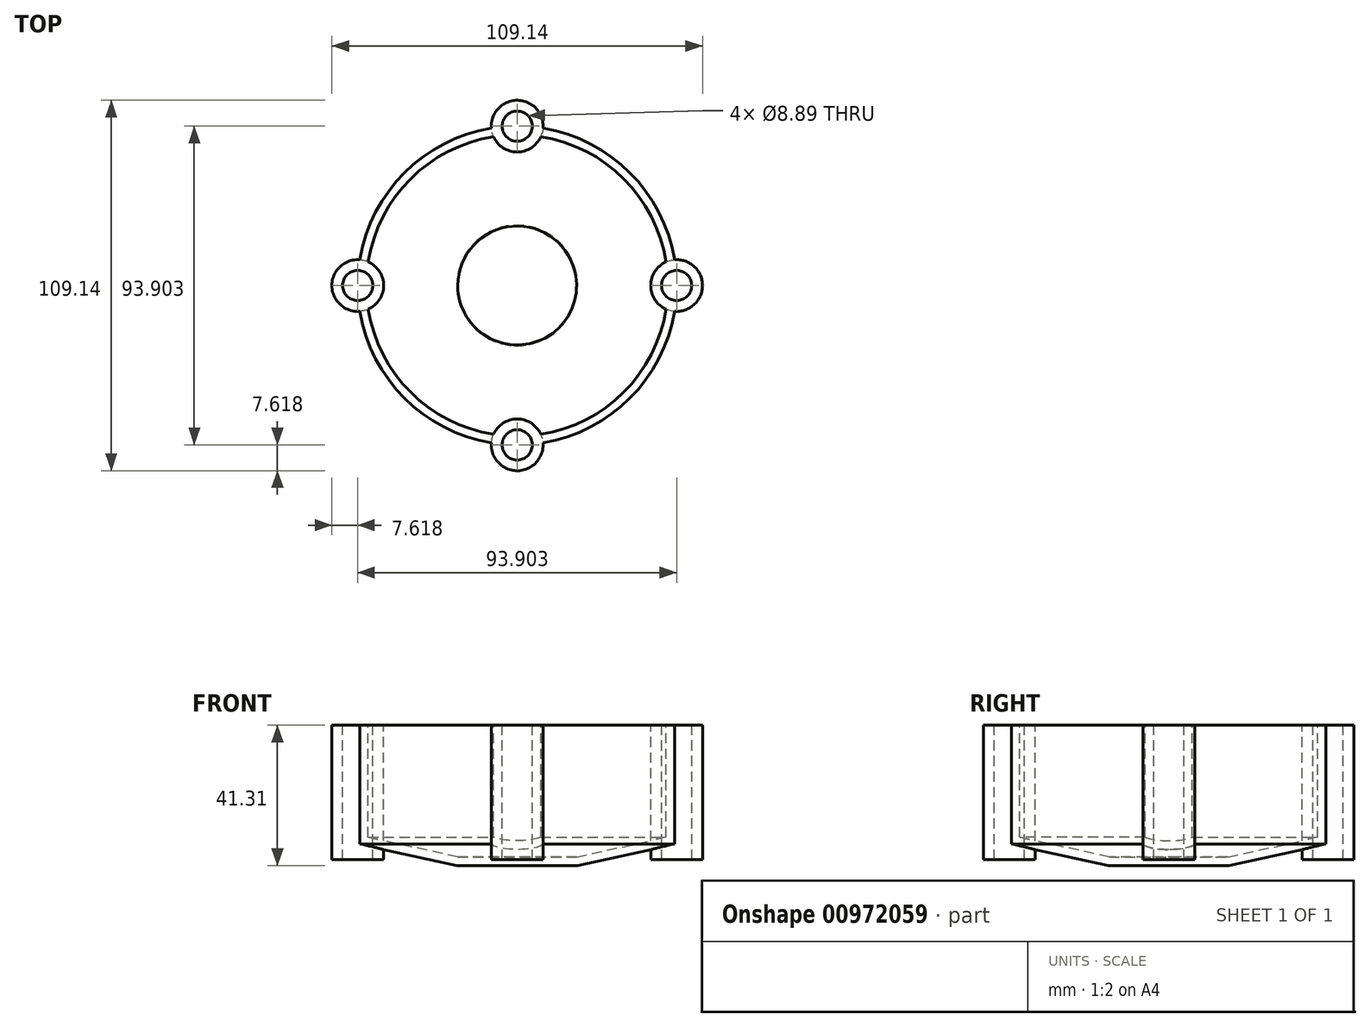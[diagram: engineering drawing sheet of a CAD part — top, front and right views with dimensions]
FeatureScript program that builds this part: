
annotation { "Feature Type Name" : "Feature", "Feature Type Description" : "" }
export const myFeature = defineFeature(function(context is Context, id is Id, definition is map)
    precondition{}
    {
        {
            var Q0;
            Q0=qCreatedBy(makeId("Front.planeOp"),FACE);
            var sketch = newSketch(context, id + "F0", { "sketchPlane" : qUnion([Q0])});
            skLineSegment(sketch, "E0", {"start": v(0, 0) * mm, "end": v(0, 38.77) * mm, "construction": true});
            skLineSegment(sketch, "E1", {"start": v(0, 0) * mm, "end": v(17.5, 0) * mm});
            skLineSegment(sketch, "E2", {"start": v(17.5, 0) * mm, "end": v(44.41, 5.85) * mm});
            skLineSegment(sketch, "E3", {"start": v(44.41, 5.85) * mm, "end": v(44.41, 38.77) * mm});
            skLineSegment(sketch, "E4.0", {"start": v(46.95, 3.8) * mm, "end": v(46.95, 38.77) * mm});
            skLineSegment(sketch, "E4.1", {"start": v(17.77, -2.54) * mm, "end": v(46.95, 3.8) * mm});
            skLineSegment(sketch, "E4.2", {"start": v(0, -2.54) * mm, "end": v(17.77, -2.54) * mm});
            skLineSegment(sketch, "E5", {"start": v(46.95, 38.77) * mm, "end": v(44.41, 38.77) * mm});
            skLineSegment(sketch, "E6", {"start": v(0, 0) * mm, "end": v(0, -2.54) * mm});
            skSolve(sketch);
        }
        {
            var Q0;
            Q0=makeQuery(id+"F0.imprint","IMPRINT",FACE,{"disambiguationData":[TD([[makeQuery(id+"F0.imprint","IMPRINT",EDGE,{"derivedFrom":sQuery(id+"F0.wireOp",EDGE,"E1")}),-1.0]])]});
            var Q1;
            Q1=sQuery(id+"F0.wireOp",EDGE,"E0");
            revolve(context, id + "F1", {"surfaceOperationType" : NewSurfaceOperationType.NEW, "entities" : qUnion([Q0]), "axis" : qUnion([Q1]), "revolveType" : RevolveType.FULL});
        }
        {
            var Q0;
            Q0=makeQuery(id+"F1.opRevolve","SWEPT_FACE",FACE,{"disambiguationData":[OSD([sQuery(id+"F0.wireOp",EDGE,"E5")])]});
            var sketch = newSketch(context, id + "F2", { "sketchPlane" : qUnion([Q0])});
            skCircle(sketch, "E7", {"center": v(0, -46.95) * mm, "radius": 7.62 * mm});
            skCircle(sketch, "E8", {"center": v(46.95, 0) * mm, "radius": 7.62 * mm});
            skCircle(sketch, "E9", {"center": v(0, 46.95) * mm, "radius": 7.62 * mm});
            skCircle(sketch, "E10", {"center": v(-46.95, 0) * mm, "radius": 7.62 * mm});
            skSolve(sketch);
        }
        {
            var Q0;
            {var subQ0=sQuery(id+"F2.wireOp",EDGE,"E7");var subQ1=makeQuery(id+"F1.opRevolve","SWEPT_EDGE",EDGE,{"disambiguationData":[OSD([sQuery(id+"F0.wireOp",EDGE,"E4.0"),sQuery(id+"F0.wireOp",EDGE,"E5")])]});var subQ2=makeQuery(id+"F2.imprint","INTERSECT",VERTEX,{"disambiguationData":[OD(0.0)],"derivedFrom":[subQ1,subQ0]});Q0=makeQuery(id+"F2.imprint","IMPRINT",FACE,{"disambiguationData":[TD([[makeQuery(id+"F2.imprint","IMPRINT",EDGE,{"disambiguationData":[TD([[subQ2,1.0]])],"derivedFrom":subQ0}),1.0]])]});}
            var Q1;
            {var subQ0=sQuery(id+"F2.wireOp",EDGE,"E9");var subQ1=makeQuery(id+"F1.opRevolve","SWEPT_EDGE",EDGE,{"disambiguationData":[OSD([sQuery(id+"F0.wireOp",EDGE,"E4.0"),sQuery(id+"F0.wireOp",EDGE,"E5")])]});var subQ2=makeQuery(id+"F2.imprint","INTERSECT",VERTEX,{"disambiguationData":[OD(0.0)],"derivedFrom":[subQ1,subQ0]});Q1=makeQuery(id+"F2.imprint","IMPRINT",FACE,{"disambiguationData":[TD([[makeQuery(id+"F2.imprint","IMPRINT",EDGE,{"disambiguationData":[TD([[subQ2,1.0]])],"derivedFrom":subQ0}),1.0]])]});}
            var Q2;
            {var subQ0=sQuery(id+"F2.wireOp",EDGE,"E10");var subQ1=makeQuery(id+"F1.opRevolve","SWEPT_EDGE",EDGE,{"disambiguationData":[OSD([sQuery(id+"F0.wireOp",EDGE,"E4.0"),sQuery(id+"F0.wireOp",EDGE,"E5")])]});var subQ2=makeQuery(id+"F2.imprint","INTERSECT",VERTEX,{"disambiguationData":[OD(0.0)],"derivedFrom":[subQ1,subQ0]});Q2=makeQuery(id+"F2.imprint","IMPRINT",FACE,{"disambiguationData":[TD([[makeQuery(id+"F2.imprint","IMPRINT",EDGE,{"disambiguationData":[TD([[subQ2,-1.0]])],"derivedFrom":subQ0}),1.0]])]});}
            var Q3;
            {var subQ0=sQuery(id+"F2.wireOp",EDGE,"E7");var subQ1=makeQuery(id+"F1.opRevolve","SWEPT_EDGE",EDGE,{"disambiguationData":[OSD([sQuery(id+"F0.wireOp",EDGE,"E3"),sQuery(id+"F0.wireOp",EDGE,"E5")])]});var subQ2=makeQuery(id+"F2.imprint","INTERSECT",VERTEX,{"disambiguationData":[OD(0.0)],"derivedFrom":[subQ1,subQ0]});Q3=makeQuery(id+"F2.imprint","IMPRINT",FACE,{"disambiguationData":[TD([[makeQuery(id+"F2.imprint","IMPRINT",EDGE,{"disambiguationData":[TD([[subQ2,-1.0]])],"derivedFrom":subQ0}),1.0]])]});}
            var Q4;
            {var subQ0=sQuery(id+"F2.wireOp",EDGE,"E8");var subQ1=makeQuery(id+"F1.opRevolve","SWEPT_EDGE",EDGE,{"disambiguationData":[OSD([sQuery(id+"F0.wireOp",EDGE,"E3"),sQuery(id+"F0.wireOp",EDGE,"E5")])]});var subQ2=makeQuery(id+"F2.imprint","INTERSECT",VERTEX,{"disambiguationData":[OD(0.0)],"derivedFrom":[subQ1,subQ0]});Q4=makeQuery(id+"F2.imprint","IMPRINT",FACE,{"disambiguationData":[TD([[makeQuery(id+"F2.imprint","IMPRINT",EDGE,{"disambiguationData":[TD([[subQ2,-1.0]])],"derivedFrom":subQ0}),1.0]])]});}
            var Q5;
            {var subQ0=sQuery(id+"F2.wireOp",EDGE,"E9");var subQ1=makeQuery(id+"F1.opRevolve","SWEPT_EDGE",EDGE,{"disambiguationData":[OSD([sQuery(id+"F0.wireOp",EDGE,"E3"),sQuery(id+"F0.wireOp",EDGE,"E5")])]});var subQ2=makeQuery(id+"F2.imprint","INTERSECT",VERTEX,{"disambiguationData":[OD(0.0)],"derivedFrom":[subQ1,subQ0]});Q5=makeQuery(id+"F2.imprint","IMPRINT",FACE,{"disambiguationData":[TD([[makeQuery(id+"F2.imprint","IMPRINT",EDGE,{"disambiguationData":[TD([[subQ2,-1.0]])],"derivedFrom":subQ0}),1.0]])]});}
            var Q6;
            {var subQ0=sQuery(id+"F2.wireOp",EDGE,"E10");var subQ1=makeQuery(id+"F1.opRevolve","SWEPT_EDGE",EDGE,{"disambiguationData":[OSD([sQuery(id+"F0.wireOp",EDGE,"E3"),sQuery(id+"F0.wireOp",EDGE,"E5")])]});var subQ2=makeQuery(id+"F2.imprint","INTERSECT",VERTEX,{"disambiguationData":[OD(0.0)],"derivedFrom":[subQ1,subQ0]});Q6=makeQuery(id+"F2.imprint","IMPRINT",FACE,{"disambiguationData":[TD([[makeQuery(id+"F2.imprint","IMPRINT",EDGE,{"disambiguationData":[TD([[subQ2,1.0]])],"derivedFrom":subQ0}),1.0]])]});}
            var Q7;
            {var subQ0=sQuery(id+"F2.wireOp",EDGE,"E7");var subQ1=sQuery(id+"F0.wireOp",EDGE,"E5");var subQ2=makeQuery(id+"F1.opRevolve","SWEPT_EDGE",EDGE,{"disambiguationData":[OSD([sQuery(id+"F0.wireOp",EDGE,"E4.0"),subQ1])]});var subQ3=makeQuery(id+"F2.imprint","INTERSECT",VERTEX,{"disambiguationData":[OD(0.0)],"derivedFrom":[subQ2,subQ0]});Q7=makeQuery(id+"F2.imprint","IMPRINT",FACE,{"disambiguationData":[TD([[makeQuery(id+"F2.imprint","IMPRINT",EDGE,{"disambiguationData":[TD([[subQ3,-1.0]])],"derivedFrom":subQ0}),1.0]])]});}
            var Q8;
            {var subQ0=sQuery(id+"F2.wireOp",EDGE,"E8");var subQ1=sQuery(id+"F0.wireOp",EDGE,"E5");var subQ2=makeQuery(id+"F1.opRevolve","SWEPT_EDGE",EDGE,{"disambiguationData":[OSD([sQuery(id+"F0.wireOp",EDGE,"E4.0"),subQ1])]});var subQ3=makeQuery(id+"F2.imprint","INTERSECT",VERTEX,{"disambiguationData":[OD(0.0)],"derivedFrom":[subQ2,subQ0]});Q8=makeQuery(id+"F2.imprint","IMPRINT",FACE,{"disambiguationData":[TD([[makeQuery(id+"F2.imprint","IMPRINT",EDGE,{"disambiguationData":[TD([[subQ3,-1.0]])],"derivedFrom":subQ0}),1.0]])]});}
            var Q9;
            {var subQ0=sQuery(id+"F2.wireOp",EDGE,"E9");var subQ1=sQuery(id+"F0.wireOp",EDGE,"E5");var subQ2=makeQuery(id+"F1.opRevolve","SWEPT_EDGE",EDGE,{"disambiguationData":[OSD([sQuery(id+"F0.wireOp",EDGE,"E4.0"),subQ1])]});var subQ3=makeQuery(id+"F2.imprint","INTERSECT",VERTEX,{"disambiguationData":[OD(0.0)],"derivedFrom":[subQ2,subQ0]});Q9=makeQuery(id+"F2.imprint","IMPRINT",FACE,{"disambiguationData":[TD([[makeQuery(id+"F2.imprint","IMPRINT",EDGE,{"disambiguationData":[TD([[subQ3,-1.0]])],"derivedFrom":subQ0}),1.0]])]});}
            var Q10;
            {var subQ0=sQuery(id+"F2.wireOp",EDGE,"E10");var subQ1=sQuery(id+"F0.wireOp",EDGE,"E5");var subQ2=makeQuery(id+"F1.opRevolve","SWEPT_EDGE",EDGE,{"disambiguationData":[OSD([sQuery(id+"F0.wireOp",EDGE,"E4.0"),subQ1])]});var subQ3=makeQuery(id+"F2.imprint","INTERSECT",VERTEX,{"disambiguationData":[OD(0.0)],"derivedFrom":[subQ2,subQ0]});Q10=makeQuery(id+"F2.imprint","IMPRINT",FACE,{"disambiguationData":[TD([[makeQuery(id+"F2.imprint","IMPRINT",EDGE,{"disambiguationData":[TD([[subQ3,1.0]])],"derivedFrom":subQ0}),1.0]])]});}
            var Q11;
            {var subQ0=sQuery(id+"F2.wireOp",EDGE,"E8");var subQ1=makeQuery(id+"F1.opRevolve","SWEPT_EDGE",EDGE,{"disambiguationData":[OSD([sQuery(id+"F0.wireOp",EDGE,"E4.0"),sQuery(id+"F0.wireOp",EDGE,"E5")])]});var subQ2=makeQuery(id+"F2.imprint","INTERSECT",VERTEX,{"disambiguationData":[OD(0.0)],"derivedFrom":[subQ1,subQ0]});Q11=makeQuery(id+"F2.imprint","IMPRINT",FACE,{"disambiguationData":[TD([[makeQuery(id+"F2.imprint","IMPRINT",EDGE,{"disambiguationData":[TD([[subQ2,1.0]])],"derivedFrom":subQ0}),1.0]])]});}
            extrude(context, id + "F3", {"entities" : qUnion([Q0, Q1, Q2, Q3, Q4, Q5, Q6, Q7, Q8, Q9, Q10, Q11]), "operationType" : NewBodyOperationType.ADD, "oppositeDirection" : true, "depth" : 39.62 * mm, "offsetDistance" : 25.4 * mm});
        }
        {
            var Q0;
            Q0=makeQuery(id+"F3.boolean.opBoolean","MERGE",FACE,{"derivedFrom":[makeQuery(id+"F1.opRevolve","SWEPT_FACE",FACE,{"disambiguationData":[OSD([sQuery(id+"F0.wireOp",EDGE,"E5")])]}),makeQuery(id+"F3.opExtrude","CAP_FACE",FACE,{"disambiguationData":[OSD([sQuery(id+"F2.wireOp",EDGE,"E7")])],"isStart":true}),makeQuery(id+"F3.opExtrude","CAP_FACE",FACE,{"disambiguationData":[OSD([sQuery(id+"F2.wireOp",EDGE,"E8")])],"isStart":true}),makeQuery(id+"F3.opExtrude","CAP_FACE",FACE,{"disambiguationData":[OSD([sQuery(id+"F2.wireOp",EDGE,"E9")])],"isStart":true}),makeQuery(id+"F3.opExtrude","CAP_FACE",FACE,{"disambiguationData":[OSD([sQuery(id+"F2.wireOp",EDGE,"E10")])],"isStart":true})]});
            var sketch = newSketch(context, id + "F4", { "sketchPlane" : qUnion([Q0])});
            skCircle(sketch, "E11", {"center": v(-46.95, 0) * mm, "radius": 4.45 * mm});
            skCircle(sketch, "E12", {"center": v(0, 46.95) * mm, "radius": 4.45 * mm});
            skCircle(sketch, "E13", {"center": v(46.95, 0) * mm, "radius": 4.45 * mm});
            skCircle(sketch, "E14", {"center": v(0, -46.95) * mm, "radius": 4.45 * mm});
            skSolve(sketch);
        }
        {
            var Q0;
            Q0=makeQuery(id+"F4.imprint","IMPRINT",FACE,{"disambiguationData":[TD([[makeQuery(id+"F4.imprint","IMPRINT",EDGE,{"derivedFrom":sQuery(id+"F4.wireOp",EDGE,"E11")}),1.0]])]});
            var Q1;
            Q1=makeQuery(id+"F4.imprint","IMPRINT",FACE,{"disambiguationData":[TD([[makeQuery(id+"F4.imprint","IMPRINT",EDGE,{"derivedFrom":sQuery(id+"F4.wireOp",EDGE,"E12")}),1.0]])]});
            var Q2;
            Q2=makeQuery(id+"F4.imprint","IMPRINT",FACE,{"disambiguationData":[TD([[makeQuery(id+"F4.imprint","IMPRINT",EDGE,{"derivedFrom":sQuery(id+"F4.wireOp",EDGE,"E13")}),1.0]])]});
            var Q3;
            Q3=makeQuery(id+"F4.imprint","IMPRINT",FACE,{"disambiguationData":[TD([[makeQuery(id+"F4.imprint","IMPRINT",EDGE,{"derivedFrom":sQuery(id+"F4.wireOp",EDGE,"E14")}),1.0]])]});
            extrude(context, id + "F5", {"entities" : qUnion([Q0, Q1, Q2, Q3]), "operationType" : NewBodyOperationType.REMOVE, "endBound" : BoundingType.THROUGH_ALL, "oppositeDirection" : true, "depth" : 25.4 * mm, "offsetDistance" : 25.4 * mm});
        }
    });
